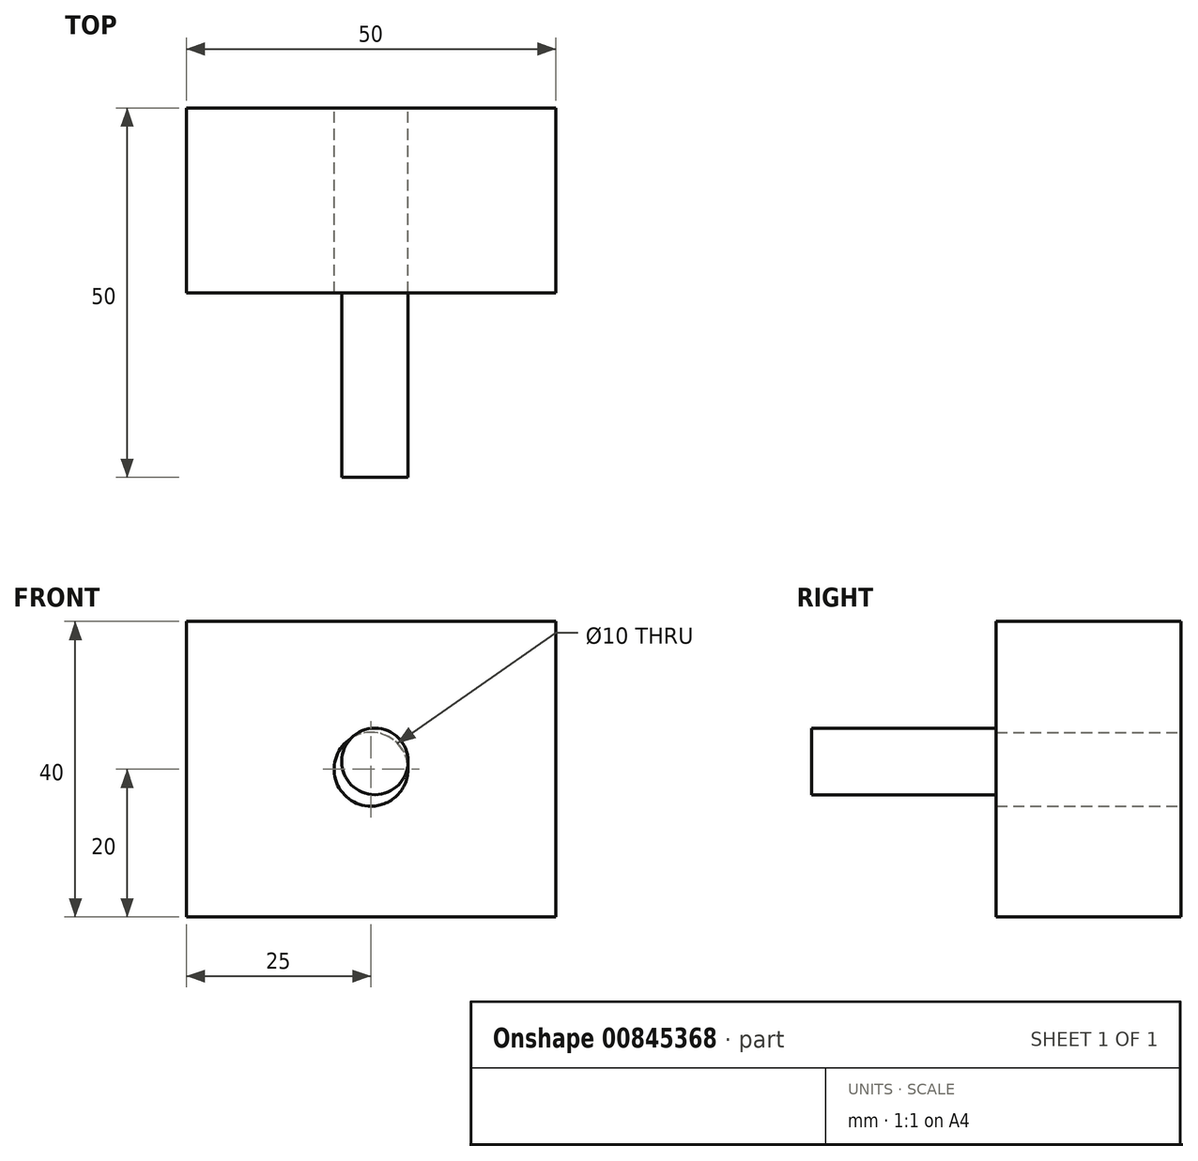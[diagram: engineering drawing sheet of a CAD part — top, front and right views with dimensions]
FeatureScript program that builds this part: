
annotation { "Feature Type Name" : "Feature", "Feature Type Description" : "" }
export const myFeature = defineFeature(function(context is Context, id is Id, definition is map)
    precondition{}
    {
        {
            var Q0;
            Q0=qCreatedBy(makeId("Front.planeOp"),FACE);
            var sketch = newSketch(context, id + "F0", { "sketchPlane" : qUnion([Q0])});
            skLineSegment(sketch, "E0.bottom", {"start": v(0, 0) * mm, "end": v(50, 0) * mm});
            skLineSegment(sketch, "E0.top", {"start": v(0, 40) * mm, "end": v(50, 40) * mm});
            skLineSegment(sketch, "E0.left", {"start": v(0, 0) * mm, "end": v(0, 40) * mm});
            skLineSegment(sketch, "E0.right", {"start": v(50, 0) * mm, "end": v(50, 40) * mm});
            skCircle(sketch, "E1", {"center": v(25, 20) * mm, "radius": 5 * mm});
            skSolve(sketch);
        }
        {
            var Q0;
            Q0 = qSketchRegion(id + "F0", true);
            extrude(context, id + "F1", {"entities" : qUnion([Q0]), "depth" : 25 * mm, "offsetDistance" : 25 * mm});
        }
        {
            var Q0;
            Q0=makeQuery(id+"F1.opExtrude","CAP_FACE",FACE,{"disambiguationData":[OSD([sQuery(id+"F0.wireOp",EDGE,"E0.bottom"),sQuery(id+"F0.wireOp",EDGE,"E0.top"),sQuery(id+"F0.wireOp",EDGE,"E0.left"),sQuery(id+"F0.wireOp",EDGE,"E0.right"),sQuery(id+"F0.wireOp",EDGE,"E1")])],"isStart":false});
            cPlane(context, id + "F2", {"entities" : qUnion([Q0]), "cplaneType" : CPlaneType.OFFSET, "offset" : 25 * mm, "width" : 150 * mm, "height" : 150 * mm});
        }
        {
            var Q0;
            Q0=qCreatedBy(id+"F2.planeOp",FACE);
            var sketch = newSketch(context, id + "F3", { "sketchPlane" : qUnion([Q0])});
            skCircle(sketch, "E2", {"center": v(25.52, 21.06) * mm, "radius": 4.5 * mm});
            skSolve(sketch);
        }
        {
            var Q0;
            Q0 = qSketchRegion(id + "F3", true);
            extrude(context, id + "F4", {"entities" : qUnion([Q0]), "oppositeDirection" : true, "depth" : 25 * mm, "offsetDistance" : 25 * mm});
        }
    });
